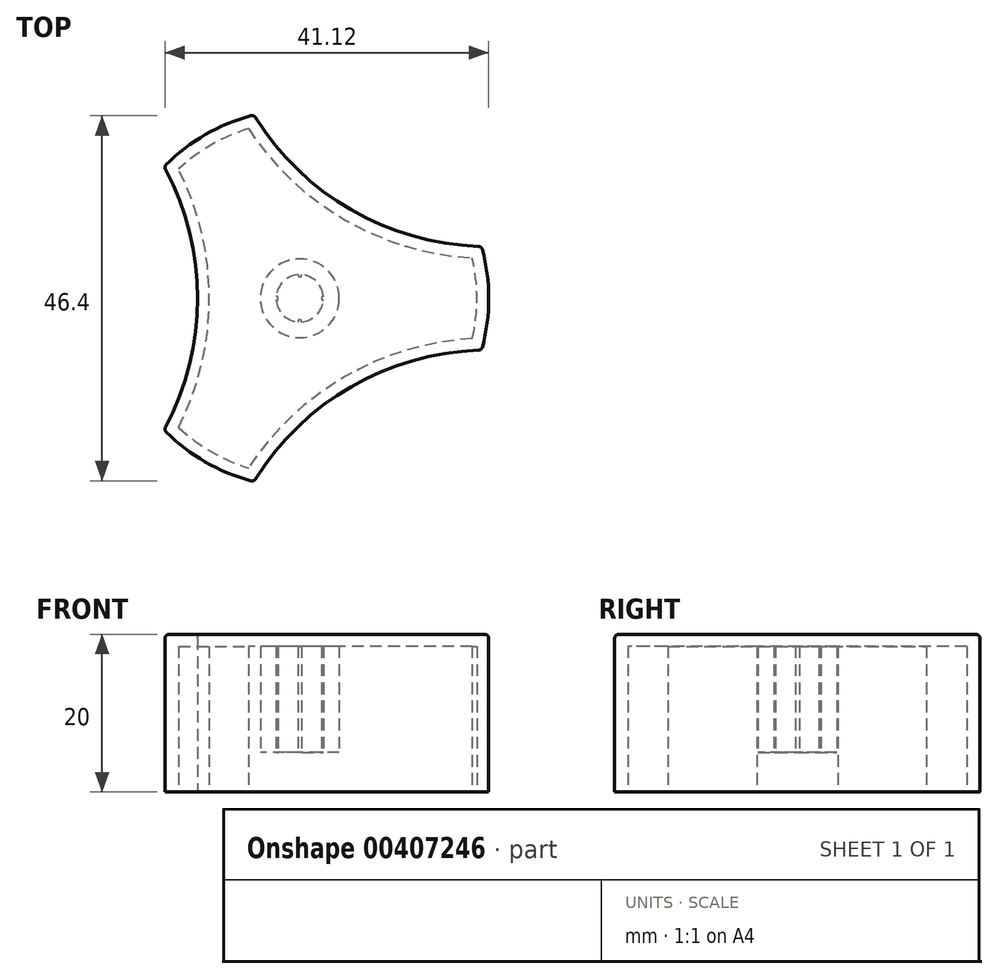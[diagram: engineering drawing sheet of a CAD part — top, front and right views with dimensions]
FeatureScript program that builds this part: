
annotation { "Feature Type Name" : "Feature", "Feature Type Description" : "" }
export const myFeature = defineFeature(function(context is Context, id is Id, definition is map)
    precondition{}
    {
        {
            var Q0;
            Q0=qCreatedBy(makeId("Top.planeOp"),FACE);
            var sketch = newSketch(context, id + "F0", { "sketchPlane" : qUnion([Q0])});
            skLineSegment(sketch, "E0", {"start": v(0, 0) * mm, "end": v(-48, 0) * mm, "construction": true});
            skCircle(sketch, "E1", {"center": v(-48, 0) * mm, "radius": 35 * mm});
            skCircle(sketch, "E2.1.0", {"center": v(24, -41.57) * mm, "radius": 35 * mm});
            skCircle(sketch, "E2.2.0", {"center": v(24, 41.57) * mm, "radius": 35 * mm});
            skPoint(sketch, "E2.center", {"position": v(0, 0) * mm});
            skLineSegment(sketch, "E3", {"start": v(24, -41.57) * mm, "end": v(-48, 0) * mm, "construction": true});
            skCircle(sketch, "E4", {"center": v(0, 0) * mm, "radius": 24 * mm});
            skCircle(sketch, "E5", {"center": v(0, 0) * mm, "radius": 3 * mm});
            skCircle(sketch, "E6", {"center": v(0, 0) * mm, "radius": 5 * mm});
            skPoint(sketch, "E7", {"position": v(-3, 0) * mm});
            skCircle(sketch, "E8", {"center": v(-3, 0) * mm, "radius": 0.25 * mm});
            skCircle(sketch, "E9.1.0", {"center": v(0, -3) * mm, "radius": 0.25 * mm});
            skCircle(sketch, "E9.2.0", {"center": v(3, 0) * mm, "radius": 0.25 * mm});
            skCircle(sketch, "E9.3.0", {"center": v(0, 3) * mm, "radius": 0.25 * mm});
            skSolve(sketch);
        }
        {
            var Q0;
            {var subQ0=sQuery(id+"F0.wireOp",EDGE,"0686783e-501e-415c-a183-79f28aa02af2.1");var subQ6=sQuery(id+"F0.wireOp",EDGE,"E1");var subQ10=makeQuery(id+"F0.imprint","INTERSECT",VERTEX,{"derivedFrom":[subQ6,subQ0]});Q0=makeQuery(id+"F0.imprint","IMPRINT",FACE,{"disambiguationData":[TD([[makeQuery(id+"F0.imprint","IMPRINT",EDGE,{"disambiguationData":[TD([[subQ10,1.0]])],"derivedFrom":subQ6}),-1.0]])]});}
            var Q1;
            Q1=makeQuery(id+"F0.imprint","IMPRINT",FACE,{"disambiguationData":[TD([[makeQuery(id+"F0.imprint","IMPRINT",EDGE,{"derivedFrom":sQuery(id+"F0.wireOp",EDGE,"E5")}),-1.0]])]});
            var Q2;
            {var subQ0=sQuery(id+"F0.wireOp",EDGE,"E8");var subQ1=sQuery(id+"F0.wireOp",EDGE,"E5");var subQ2=makeQuery(id+"F0.imprint","INTERSECT",VERTEX,{"disambiguationData":[OD(0.0)],"derivedFrom":[subQ1,subQ0]});Q2=makeQuery(id+"F0.imprint","IMPRINT",FACE,{"disambiguationData":[TD([[makeQuery(id+"F0.imprint","IMPRINT",EDGE,{"disambiguationData":[TD([[subQ2,-1.0]])],"derivedFrom":subQ1}),-1.0]])]});}
            var Q3;
            {var subQ0=sQuery(id+"F0.wireOp",EDGE,"E9.1.0");var subQ1=sQuery(id+"F0.wireOp",EDGE,"E5");var subQ2=makeQuery(id+"F0.imprint","INTERSECT",VERTEX,{"disambiguationData":[OD(0.0)],"derivedFrom":[subQ1,subQ0]});Q3=makeQuery(id+"F0.imprint","IMPRINT",FACE,{"disambiguationData":[TD([[makeQuery(id+"F0.imprint","IMPRINT",EDGE,{"disambiguationData":[TD([[subQ2,-1.0]])],"derivedFrom":subQ1}),-1.0]])]});}
            var Q4;
            {var subQ1=sQuery(id+"F0.wireOp",EDGE,"E5");var subQ8=sQuery(id+"F0.wireOp",EDGE,"E9.3.0");var subQ11=makeQuery(id+"F0.imprint","INTERSECT",VERTEX,{"disambiguationData":[OD(0.0)],"derivedFrom":[subQ1,subQ8]});Q4=makeQuery(id+"F0.imprint","IMPRINT",FACE,{"disambiguationData":[TD([[makeQuery(id+"F0.imprint","IMPRINT",EDGE,{"disambiguationData":[TD([[subQ11,1.0]])],"derivedFrom":subQ1}),1.0]])]});}
            var Q5;
            {var subQ0=sQuery(id+"F0.wireOp",EDGE,"E9.1.0");var subQ1=sQuery(id+"F0.wireOp",EDGE,"E5");var subQ2=makeQuery(id+"F0.imprint","INTERSECT",VERTEX,{"disambiguationData":[OD(0.0)],"derivedFrom":[subQ1,subQ0]});Q5=makeQuery(id+"F0.imprint","IMPRINT",FACE,{"disambiguationData":[TD([[makeQuery(id+"F0.imprint","IMPRINT",EDGE,{"disambiguationData":[TD([[subQ2,-1.0]])],"derivedFrom":subQ1}),1.0]])]});}
            var Q6;
            {var subQ0=sQuery(id+"F0.wireOp",EDGE,"E9.3.0");var subQ1=sQuery(id+"F0.wireOp",EDGE,"E5");var subQ2=makeQuery(id+"F0.imprint","INTERSECT",VERTEX,{"disambiguationData":[OD(0.0)],"derivedFrom":[subQ1,subQ0]});Q6=makeQuery(id+"F0.imprint","IMPRINT",FACE,{"disambiguationData":[TD([[makeQuery(id+"F0.imprint","IMPRINT",EDGE,{"disambiguationData":[TD([[subQ2,-1.0]])],"derivedFrom":subQ1}),1.0]])]});}
            var Q7;
            {var subQ0=sQuery(id+"F0.wireOp",EDGE,"E9.3.0");var subQ1=sQuery(id+"F0.wireOp",EDGE,"E5");var subQ2=makeQuery(id+"F0.imprint","INTERSECT",VERTEX,{"disambiguationData":[OD(0.0)],"derivedFrom":[subQ1,subQ0]});Q7=makeQuery(id+"F0.imprint","IMPRINT",FACE,{"disambiguationData":[TD([[makeQuery(id+"F0.imprint","IMPRINT",EDGE,{"disambiguationData":[TD([[subQ2,-1.0]])],"derivedFrom":subQ1}),-1.0]])]});}
            var Q8;
            {var subQ0=sQuery(id+"F0.wireOp",EDGE,"E8");var subQ1=sQuery(id+"F0.wireOp",EDGE,"E5");var subQ2=makeQuery(id+"F0.imprint","INTERSECT",VERTEX,{"disambiguationData":[OD(0.0)],"derivedFrom":[subQ1,subQ0]});Q8=makeQuery(id+"F0.imprint","IMPRINT",FACE,{"disambiguationData":[TD([[makeQuery(id+"F0.imprint","IMPRINT",EDGE,{"disambiguationData":[TD([[subQ2,-1.0]])],"derivedFrom":subQ1}),1.0]])]});}
            var Q9;
            {var subQ0=sQuery(id+"F0.wireOp",EDGE,"E9.2.0");var subQ1=sQuery(id+"F0.wireOp",EDGE,"E5");var subQ2=makeQuery(id+"F0.imprint","INTERSECT",VERTEX,{"disambiguationData":[OD(0.0)],"derivedFrom":[subQ1,subQ0]});Q9=makeQuery(id+"F0.imprint","IMPRINT",FACE,{"disambiguationData":[TD([[makeQuery(id+"F0.imprint","IMPRINT",EDGE,{"disambiguationData":[TD([[subQ2,1.0]])],"derivedFrom":subQ1}),-1.0]])]});}
            var Q10;
            {var subQ0=sQuery(id+"F0.wireOp",EDGE,"E9.2.0");var subQ1=sQuery(id+"F0.wireOp",EDGE,"E5");var subQ2=makeQuery(id+"F0.imprint","INTERSECT",VERTEX,{"disambiguationData":[OD(0.0)],"derivedFrom":[subQ1,subQ0]});Q10=makeQuery(id+"F0.imprint","IMPRINT",FACE,{"disambiguationData":[TD([[makeQuery(id+"F0.imprint","IMPRINT",EDGE,{"disambiguationData":[TD([[subQ2,1.0]])],"derivedFrom":subQ1}),1.0]])]});}
            extrude(context, id + "F1", {"entities" : qUnion([Q0, Q1, Q2, Q3, Q4, Q5, Q6, Q7, Q8, Q9, Q10]), "depth" : 20 * mm});
        }
        {
            var Q0;
            Q0=makeQuery(id+"F1.opExtrude","CAP_FACE",FACE,{"disambiguationData":[OSD([sQuery(id+"F0.wireOp",EDGE,"E1"),sQuery(id+"F0.wireOp",EDGE,"E2.1.0"),sQuery(id+"F0.wireOp",EDGE,"E2.2.0"),sQuery(id+"F0.wireOp",EDGE,"E4")])],"isStart":true});
            shell(context, id + "F2", {"entities" : qUnion([Q0]), "thickness" : 1.5 * mm});
        }
        {
            var Q0;
            Q0=makeQuery(id+"F0.imprint","IMPRINT",FACE,{"disambiguationData":[TD([[makeQuery(id+"F0.imprint","IMPRINT",EDGE,{"derivedFrom":sQuery(id+"F0.wireOp",EDGE,"E6")}),1.0]])]});
            var Q1;
            {var subQ0=sQuery(id+"F0.wireOp",EDGE,"E8");var subQ1=sQuery(id+"F0.wireOp",EDGE,"E5");var subQ2=makeQuery(id+"F0.imprint","INTERSECT",VERTEX,{"disambiguationData":[OD(0.0)],"derivedFrom":[subQ1,subQ0]});Q1=makeQuery(id+"F0.imprint","IMPRINT",FACE,{"disambiguationData":[TD([[makeQuery(id+"F0.imprint","IMPRINT",EDGE,{"disambiguationData":[TD([[subQ2,-1.0]])],"derivedFrom":subQ1}),1.0]])]});}
            var Q2;
            {var subQ0=sQuery(id+"F0.wireOp",EDGE,"E8");var subQ1=sQuery(id+"F0.wireOp",EDGE,"E5");var subQ2=makeQuery(id+"F0.imprint","INTERSECT",VERTEX,{"disambiguationData":[OD(0.0)],"derivedFrom":[subQ1,subQ0]});Q2=makeQuery(id+"F0.imprint","IMPRINT",FACE,{"disambiguationData":[TD([[makeQuery(id+"F0.imprint","IMPRINT",EDGE,{"disambiguationData":[TD([[subQ2,-1.0]])],"derivedFrom":subQ1}),-1.0]])]});}
            var Q3;
            {var subQ0=sQuery(id+"F0.wireOp",EDGE,"E9.3.0");var subQ1=sQuery(id+"F0.wireOp",EDGE,"E5");var subQ2=makeQuery(id+"F0.imprint","INTERSECT",VERTEX,{"disambiguationData":[OD(0.0)],"derivedFrom":[subQ1,subQ0]});Q3=makeQuery(id+"F0.imprint","IMPRINT",FACE,{"disambiguationData":[TD([[makeQuery(id+"F0.imprint","IMPRINT",EDGE,{"disambiguationData":[TD([[subQ2,-1.0]])],"derivedFrom":subQ1}),1.0]])]});}
            var Q4;
            {var subQ0=sQuery(id+"F0.wireOp",EDGE,"E9.3.0");var subQ1=sQuery(id+"F0.wireOp",EDGE,"E5");var subQ2=makeQuery(id+"F0.imprint","INTERSECT",VERTEX,{"disambiguationData":[OD(0.0)],"derivedFrom":[subQ1,subQ0]});Q4=makeQuery(id+"F0.imprint","IMPRINT",FACE,{"disambiguationData":[TD([[makeQuery(id+"F0.imprint","IMPRINT",EDGE,{"disambiguationData":[TD([[subQ2,-1.0]])],"derivedFrom":subQ1}),-1.0]])]});}
            var Q5;
            {var subQ0=sQuery(id+"F0.wireOp",EDGE,"E9.2.0");var subQ1=sQuery(id+"F0.wireOp",EDGE,"E5");var subQ2=makeQuery(id+"F0.imprint","INTERSECT",VERTEX,{"disambiguationData":[OD(0.0)],"derivedFrom":[subQ1,subQ0]});Q5=makeQuery(id+"F0.imprint","IMPRINT",FACE,{"disambiguationData":[TD([[makeQuery(id+"F0.imprint","IMPRINT",EDGE,{"disambiguationData":[TD([[subQ2,1.0]])],"derivedFrom":subQ1}),1.0]])]});}
            var Q6;
            {var subQ0=sQuery(id+"F0.wireOp",EDGE,"E9.1.0");var subQ1=sQuery(id+"F0.wireOp",EDGE,"E5");var subQ2=makeQuery(id+"F0.imprint","INTERSECT",VERTEX,{"disambiguationData":[OD(0.0)],"derivedFrom":[subQ1,subQ0]});Q6=makeQuery(id+"F0.imprint","IMPRINT",FACE,{"disambiguationData":[TD([[makeQuery(id+"F0.imprint","IMPRINT",EDGE,{"disambiguationData":[TD([[subQ2,-1.0]])],"derivedFrom":subQ1}),1.0]])]});}
            var Q7;
            {var subQ0=sQuery(id+"F0.wireOp",EDGE,"E9.1.0");var subQ1=sQuery(id+"F0.wireOp",EDGE,"E5");var subQ2=makeQuery(id+"F0.imprint","INTERSECT",VERTEX,{"disambiguationData":[OD(0.0)],"derivedFrom":[subQ1,subQ0]});Q7=makeQuery(id+"F0.imprint","IMPRINT",FACE,{"disambiguationData":[TD([[makeQuery(id+"F0.imprint","IMPRINT",EDGE,{"disambiguationData":[TD([[subQ2,-1.0]])],"derivedFrom":subQ1}),-1.0]])]});}
            var Q8;
            {var subQ0=sQuery(id+"F0.wireOp",EDGE,"E9.2.0");var subQ1=sQuery(id+"F0.wireOp",EDGE,"E5");var subQ2=makeQuery(id+"F0.imprint","INTERSECT",VERTEX,{"disambiguationData":[OD(0.0)],"derivedFrom":[subQ1,subQ0]});Q8=makeQuery(id+"F0.imprint","IMPRINT",FACE,{"disambiguationData":[TD([[makeQuery(id+"F0.imprint","IMPRINT",EDGE,{"disambiguationData":[TD([[subQ2,1.0]])],"derivedFrom":subQ1}),-1.0]])]});}
            extrude(context, id + "F3", {"entities" : qUnion([Q0, Q1, Q2, Q3, Q4, Q5, Q6, Q7, Q8]), "operationType" : NewBodyOperationType.ADD, "depth" : 19 * mm});
        }
        {
            var Q0;
            Q0=makeQuery(id+"F1.opExtrude","CAP_EDGE",EDGE,{"disambiguationData":[OSD([sQuery(id+"F0.wireOp",EDGE,"E2.2.0")])],"isStart":false});
            var Q1;
            {var subQ0=sQuery(id+"F0.wireOp",EDGE,"E4");Q1=makeQuery(id+"F1.opExtrude","CAP_EDGE",EDGE,{"disambiguationData":[OSD([subQ0]),TDD([makeQuery(id+"F0.imprint","IMPRINT",EDGE,{"disambiguationData":[TD([[makeQuery(id+"F0.imprint","INTERSECT",VERTEX,{"disambiguationData":[OD(1.0)],"derivedFrom":[sQuery(id+"F0.wireOp",EDGE,"E2.1.0"),subQ0]}),-1.0]])],"derivedFrom":subQ0})])],"isStart":false});}
            var Q2;
            Q2=makeQuery(id+"F1.opExtrude","CAP_EDGE",EDGE,{"disambiguationData":[OSD([sQuery(id+"F0.wireOp",EDGE,"E2.1.0")])],"isStart":false});
            var Q3;
            {var subQ0=sQuery(id+"F0.wireOp",EDGE,"E4");Q3=makeQuery(id+"F1.opExtrude","CAP_EDGE",EDGE,{"disambiguationData":[OSD([subQ0]),TDD([makeQuery(id+"F0.imprint","IMPRINT",EDGE,{"disambiguationData":[TD([[makeQuery(id+"F0.imprint","INTERSECT",VERTEX,{"disambiguationData":[OD(1.0)],"derivedFrom":[sQuery(id+"F0.wireOp",EDGE,"E1"),subQ0]}),-1.0]])],"derivedFrom":subQ0})])],"isStart":false});}
            var Q4;
            Q4=makeQuery(id+"F1.opExtrude","CAP_EDGE",EDGE,{"disambiguationData":[OSD([sQuery(id+"F0.wireOp",EDGE,"E1")])],"isStart":false});
            var Q5;
            {var subQ0=sQuery(id+"F0.wireOp",EDGE,"E4");Q5=makeQuery(id+"F1.opExtrude","CAP_EDGE",EDGE,{"disambiguationData":[OSD([subQ0]),TDD([makeQuery(id+"F0.imprint","IMPRINT",EDGE,{"disambiguationData":[TD([[makeQuery(id+"F0.imprint","INTERSECT",VERTEX,{"disambiguationData":[OD(0.0)],"derivedFrom":[sQuery(id+"F0.wireOp",EDGE,"E1"),subQ0]}),1.0]])],"derivedFrom":subQ0})])],"isStart":false});}
            var Q6;
            {var subQ0=sQuery(id+"F0.wireOp",EDGE,"E4");var subQ1=sQuery(id+"F0.wireOp",EDGE,"E2.2.0");Q6=makeQuery(id+"F1.opExtrude","SWEPT_EDGE",EDGE,{"disambiguationData":[OSD([subQ1,subQ0]),TDD([makeQuery(id+"F0.imprint","INTERSECT",VERTEX,{"disambiguationData":[OD(1.0)],"derivedFrom":[subQ1,subQ0]})])]});}
            var Q7;
            {var subQ0=sQuery(id+"F0.wireOp",EDGE,"E4");var subQ1=sQuery(id+"F0.wireOp",EDGE,"E2.2.0");Q7=makeQuery(id+"F1.opExtrude","SWEPT_EDGE",EDGE,{"disambiguationData":[OSD([subQ1,subQ0]),TDD([makeQuery(id+"F0.imprint","INTERSECT",VERTEX,{"disambiguationData":[OD(0.0)],"derivedFrom":[subQ1,subQ0]})])]});}
            var Q8;
            {var subQ0=sQuery(id+"F0.wireOp",EDGE,"E4");var subQ1=sQuery(id+"F0.wireOp",EDGE,"E1");Q8=makeQuery(id+"F1.opExtrude","SWEPT_EDGE",EDGE,{"disambiguationData":[OSD([subQ1,subQ0]),TDD([makeQuery(id+"F0.imprint","INTERSECT",VERTEX,{"disambiguationData":[OD(0.0)],"derivedFrom":[subQ1,subQ0]})])]});}
            var Q9;
            {var subQ0=sQuery(id+"F0.wireOp",EDGE,"E4");var subQ1=sQuery(id+"F0.wireOp",EDGE,"E1");Q9=makeQuery(id+"F1.opExtrude","SWEPT_EDGE",EDGE,{"disambiguationData":[OSD([subQ1,subQ0]),TDD([makeQuery(id+"F0.imprint","INTERSECT",VERTEX,{"disambiguationData":[OD(1.0)],"derivedFrom":[subQ1,subQ0]})])]});}
            var Q10;
            {var subQ0=sQuery(id+"F0.wireOp",EDGE,"E4");var subQ1=sQuery(id+"F0.wireOp",EDGE,"E2.1.0");Q10=makeQuery(id+"F1.opExtrude","SWEPT_EDGE",EDGE,{"disambiguationData":[OSD([subQ1,subQ0]),TDD([makeQuery(id+"F0.imprint","INTERSECT",VERTEX,{"disambiguationData":[OD(0.0)],"derivedFrom":[subQ1,subQ0]})])]});}
            var Q11;
            {var subQ0=sQuery(id+"F0.wireOp",EDGE,"E4");var subQ1=sQuery(id+"F0.wireOp",EDGE,"E2.1.0");Q11=makeQuery(id+"F1.opExtrude","SWEPT_EDGE",EDGE,{"disambiguationData":[OSD([subQ1,subQ0]),TDD([makeQuery(id+"F0.imprint","INTERSECT",VERTEX,{"disambiguationData":[OD(1.0)],"derivedFrom":[subQ1,subQ0]})])]});}
            fillet(context, id + "F4", {"entities" : qUnion([Q0, Q1, Q2, Q3, Q4, Q5, Q6, Q7, Q8, Q9, Q10, Q11]), "radius" : .5 * mm, "tangentPropagation" : true, "allowEdgeOverflow" : false});
        }
        {
            var Q0;
            Q0=makeQuery(id+"F0.imprint","IMPRINT",FACE,{"disambiguationData":[TD([[makeQuery(id+"F0.imprint","IMPRINT",EDGE,{"derivedFrom":sQuery(id+"F0.wireOp",EDGE,"E5")}),-1.0]])]});
            var Q1;
            {var subQ0=sQuery(id+"F0.wireOp",EDGE,"E8");var subQ1=sQuery(id+"F0.wireOp",EDGE,"E5");var subQ2=makeQuery(id+"F0.imprint","INTERSECT",VERTEX,{"disambiguationData":[OD(0.0)],"derivedFrom":[subQ1,subQ0]});Q1=makeQuery(id+"F0.imprint","IMPRINT",FACE,{"disambiguationData":[TD([[makeQuery(id+"F0.imprint","IMPRINT",EDGE,{"disambiguationData":[TD([[subQ2,-1.0]])],"derivedFrom":subQ1}),-1.0]])]});}
            var Q2;
            {var subQ0=sQuery(id+"F0.wireOp",EDGE,"E9.1.0");var subQ1=sQuery(id+"F0.wireOp",EDGE,"E5");var subQ2=makeQuery(id+"F0.imprint","INTERSECT",VERTEX,{"disambiguationData":[OD(0.0)],"derivedFrom":[subQ1,subQ0]});Q2=makeQuery(id+"F0.imprint","IMPRINT",FACE,{"disambiguationData":[TD([[makeQuery(id+"F0.imprint","IMPRINT",EDGE,{"disambiguationData":[TD([[subQ2,-1.0]])],"derivedFrom":subQ1}),1.0]])]});}
            var Q3;
            {var subQ0=sQuery(id+"F0.wireOp",EDGE,"E9.1.0");var subQ1=sQuery(id+"F0.wireOp",EDGE,"E5");var subQ2=makeQuery(id+"F0.imprint","INTERSECT",VERTEX,{"disambiguationData":[OD(0.0)],"derivedFrom":[subQ1,subQ0]});Q3=makeQuery(id+"F0.imprint","IMPRINT",FACE,{"disambiguationData":[TD([[makeQuery(id+"F0.imprint","IMPRINT",EDGE,{"disambiguationData":[TD([[subQ2,-1.0]])],"derivedFrom":subQ1}),-1.0]])]});}
            var Q4;
            {var subQ0=sQuery(id+"F0.wireOp",EDGE,"E8");var subQ1=sQuery(id+"F0.wireOp",EDGE,"E5");var subQ2=makeQuery(id+"F0.imprint","INTERSECT",VERTEX,{"disambiguationData":[OD(0.0)],"derivedFrom":[subQ1,subQ0]});Q4=makeQuery(id+"F0.imprint","IMPRINT",FACE,{"disambiguationData":[TD([[makeQuery(id+"F0.imprint","IMPRINT",EDGE,{"disambiguationData":[TD([[subQ2,-1.0]])],"derivedFrom":subQ1}),1.0]])]});}
            var Q5;
            {var subQ0=sQuery(id+"F0.wireOp",EDGE,"E9.3.0");var subQ1=sQuery(id+"F0.wireOp",EDGE,"E5");var subQ2=makeQuery(id+"F0.imprint","INTERSECT",VERTEX,{"disambiguationData":[OD(0.0)],"derivedFrom":[subQ1,subQ0]});Q5=makeQuery(id+"F0.imprint","IMPRINT",FACE,{"disambiguationData":[TD([[makeQuery(id+"F0.imprint","IMPRINT",EDGE,{"disambiguationData":[TD([[subQ2,-1.0]])],"derivedFrom":subQ1}),1.0]])]});}
            var Q6;
            {var subQ0=sQuery(id+"F0.wireOp",EDGE,"E9.3.0");var subQ1=sQuery(id+"F0.wireOp",EDGE,"E5");var subQ2=makeQuery(id+"F0.imprint","INTERSECT",VERTEX,{"disambiguationData":[OD(0.0)],"derivedFrom":[subQ1,subQ0]});Q6=makeQuery(id+"F0.imprint","IMPRINT",FACE,{"disambiguationData":[TD([[makeQuery(id+"F0.imprint","IMPRINT",EDGE,{"disambiguationData":[TD([[subQ2,-1.0]])],"derivedFrom":subQ1}),-1.0]])]});}
            var Q7;
            {var subQ0=sQuery(id+"F0.wireOp",EDGE,"E9.2.0");var subQ1=sQuery(id+"F0.wireOp",EDGE,"E5");var subQ2=makeQuery(id+"F0.imprint","INTERSECT",VERTEX,{"disambiguationData":[OD(0.0)],"derivedFrom":[subQ1,subQ0]});Q7=makeQuery(id+"F0.imprint","IMPRINT",FACE,{"disambiguationData":[TD([[makeQuery(id+"F0.imprint","IMPRINT",EDGE,{"disambiguationData":[TD([[subQ2,1.0]])],"derivedFrom":subQ1}),-1.0]])]});}
            var Q8;
            {var subQ0=sQuery(id+"F0.wireOp",EDGE,"E9.2.0");var subQ1=sQuery(id+"F0.wireOp",EDGE,"E5");var subQ2=makeQuery(id+"F0.imprint","INTERSECT",VERTEX,{"disambiguationData":[OD(0.0)],"derivedFrom":[subQ1,subQ0]});Q8=makeQuery(id+"F0.imprint","IMPRINT",FACE,{"disambiguationData":[TD([[makeQuery(id+"F0.imprint","IMPRINT",EDGE,{"disambiguationData":[TD([[subQ2,1.0]])],"derivedFrom":subQ1}),1.0]])]});}
            extrude(context, id + "F5", {"entities" : qUnion([Q0, Q1, Q2, Q3, Q4, Q5, Q6, Q7, Q8]), "operationType" : NewBodyOperationType.REMOVE, "depth" : 5 * mm});
        }
    });
